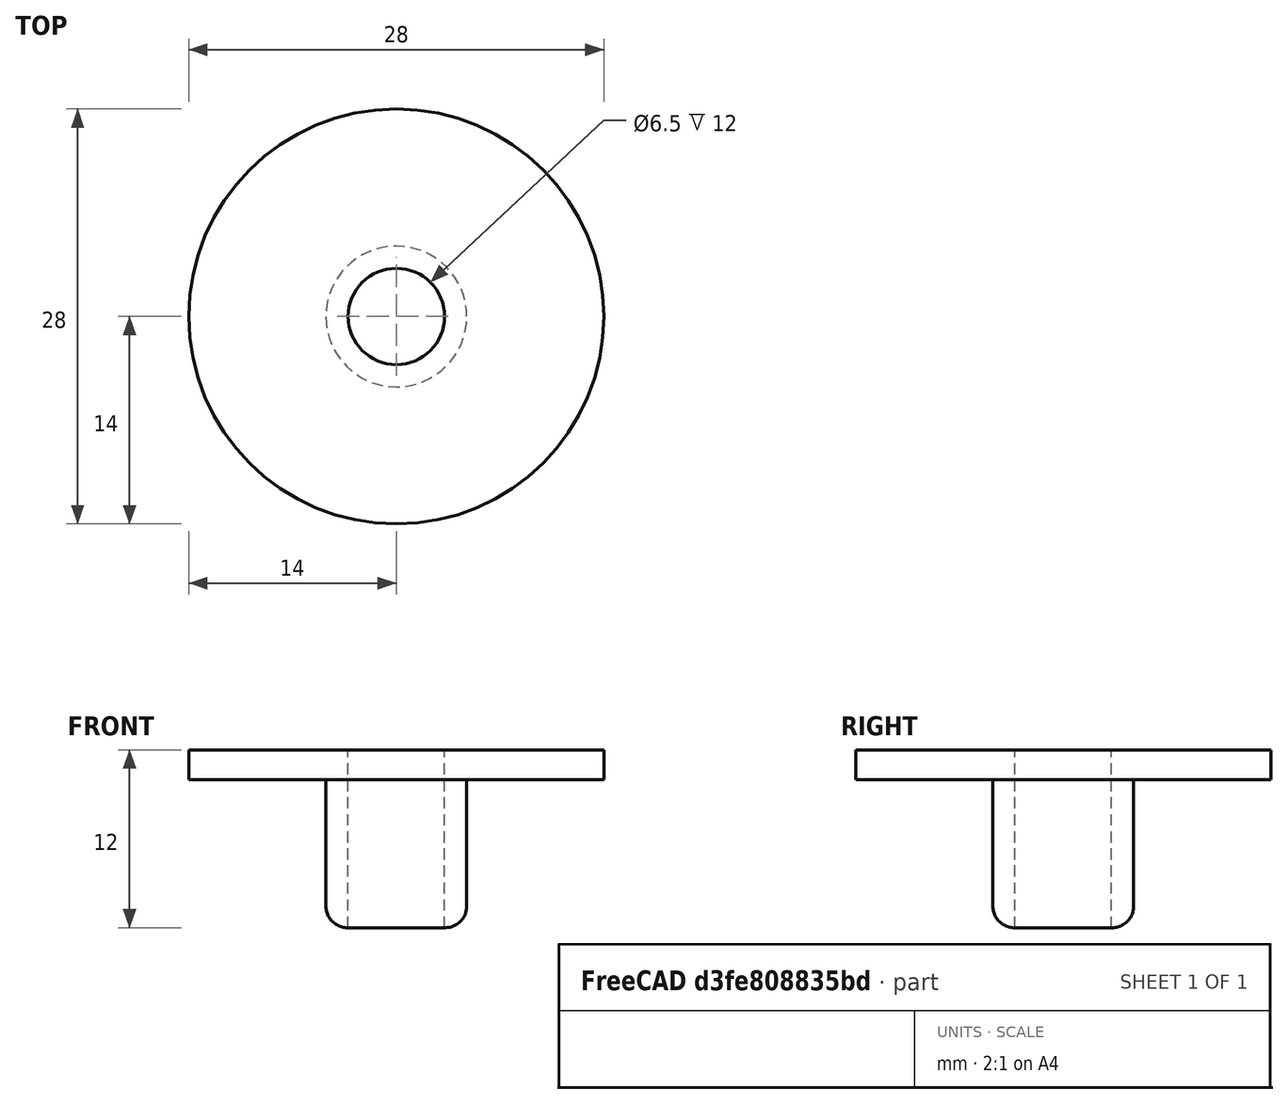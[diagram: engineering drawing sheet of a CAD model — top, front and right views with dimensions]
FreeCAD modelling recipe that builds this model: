
FCSTD DOCUMENT  (FreeCAD 1.0R39319 (Git))
Label: SodaCap
License: All rights reserved
LicenseURL: https://en.wikipedia.org/wiki/All_rights_reserved
objects: Sketcher::SketchObject×2, PartDesign::Pad×2, Mesh::Feature×1, PartDesign::Hole×1, PartDesign::Fillet×1, PartDesign::Body×1
note: 17 computed .brp shape members not serialized (recipe doc carries the construction recipe); baked Part::Feature solids carry a one-line shape summary decoded from their .brp

FEATURE [Mesh::Feature] _LiterThreads  label="2LiterThreads"
FEATURE [Sketcher::SketchObject] Sketch
  ArcFitTolerance = 1e-06
  AttachmentSupport = -> [XY_Plane]
  FullyConstrained = true
  MakeInternals = false
  MapMode = 5
  sketch-geometry (1):
    g0: Circle CenterX=0 CenterY=0 CenterZ=0 NormalX=0 NormalY=0 NormalZ=1 AngleXU=0 Radius=14
  constraints (2):
    c: Coincident(g0,g-1)
    c: Diameter(g0) = 28
FEATURE [PartDesign::Pad] Pad
  Direction = (0,0,1)
  Length = 2
  Length2 = 10
  Profile = -> Sketch
  ReferenceAxis = -> Sketch [N_Axis]
  Refine = true
  Suppressed = false
  Type = 0
FEATURE [Sketcher::SketchObject] Sketch001
  ArcFitTolerance = 1e-06
  AttachmentSupport = -> [Pad]
  FullyConstrained = true
  MakeInternals = false
  MapMode = 5
  Placement = pos=(0,0,0) rot=(1,0,0;3.14159rad)
  sketch-geometry (1):
    g0: Circle CenterX=0 CenterY=0 CenterZ=0 NormalX=0 NormalY=0 NormalZ=1 AngleXU=0 Radius=4.75
  constraints (2):
    c: Diameter(g0) = 9.5
    c: Coincident(g0,g-1)
FEATURE [PartDesign::Pad] Pad001
  BaseFeature = -> Pad
  Direction = (0,0,-1)
  Length = 10
  Length2 = 10
  Profile = -> Sketch001
  ReferenceAxis = -> Sketch001 [N_Axis]
  Refine = true
  Suppressed = false
  Type = 0
FEATURE [PartDesign::Hole] Hole
  BaseFeature = -> Pad001
  CustomThreadClearance = 0
  Depth = 25
  DepthType = 0
  Diameter = 6.5
  DrillForDepth = false
  DrillPoint = 1
  DrillPointAngle = 118
  HoleCutCountersinkAngle = 90
  HoleCutCustomValues = false
  HoleCutDepth = 0
  HoleCutDiameter = 6.1
  HoleCutType = 0
  ModelThread = false
  Profile = -> Pad001 [Face5]
  Refine = true
  Suppressed = false
  Tapered = false
  TaperedAngle = 90
  ThreadClass = 0
  ThreadDepth = 25
  ThreadDepthType = 0
  ThreadDirection = 0
  ThreadFit = 0
  ThreadSize = 0
  ThreadType = 0
  Threaded = false
  UseCustomThreadClearance = false
FEATURE [PartDesign::Fillet] Fillet
  Base = -> Hole [Edge7]
  BaseFeature = -> Hole
  Radius = 1.45
  Refine = true
  SupportTransform = false
  Suppressed = false
  UseAllEdges = false
FEATURE [PartDesign::Body] Body  label="cap"
  AllowCompound = false
  Group = -> [Sketch,Pad,Sketch001,Pad001,Hole,Fillet]
  Origin = -> Origin
  Tip = -> Fillet
